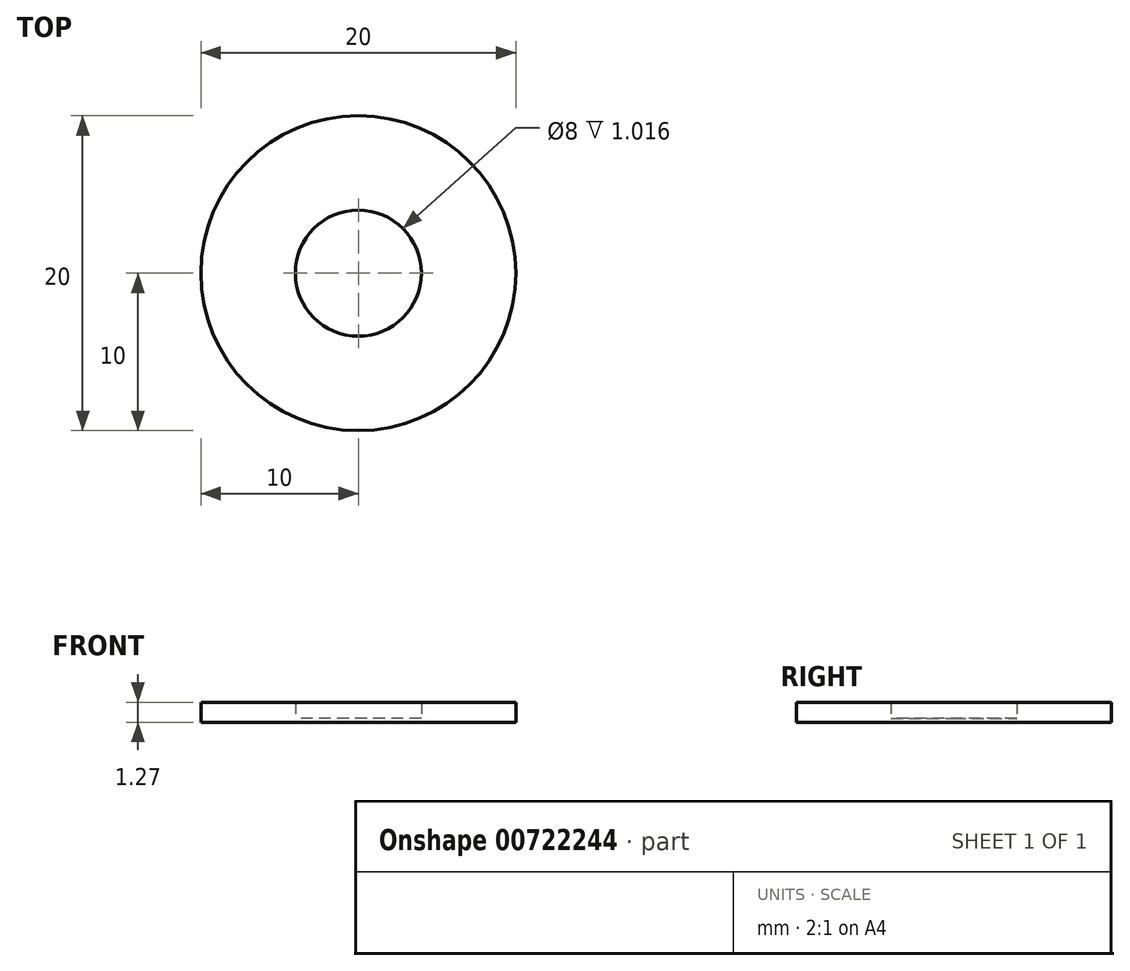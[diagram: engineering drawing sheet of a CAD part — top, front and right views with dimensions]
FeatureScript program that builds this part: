
annotation { "Feature Type Name" : "Feature", "Feature Type Description" : "" }
export const myFeature = defineFeature(function(context is Context, id is Id, definition is map)
    precondition{}
    {
        {
            var Q0;
            Q0=qCreatedBy(makeId("Top.planeOp"),FACE);
            var sketch = newSketch(context, id + "F0", { "sketchPlane" : qUnion([Q0])});
            skCircle(sketch, "E0", {"center": v(0, 0) * mm, "radius": 10 * mm});
            skCircle(sketch, "E1", {"center": v(0, 0) * mm, "radius": 4 * mm});
            skSolve(sketch);
        }
        {
            var Q0;
            Q0=qSketchRegion(id+"F0",true);
            var Q1;
            Q1=makeQuery(id+"F0.imprint","IMPRINT",FACE,{"disambiguationData":[TD([[makeQuery(id+"F0.imprint","IMPRINT",EDGE,{"derivedFrom":sQuery(id+"F0.wireOp",EDGE,"E0")}),1.0]])]});
            extrude(context, id + "F1", {"entities" : qUnion([Q0, Q1]), "depth" : 1.27 * mm, "offsetDistance" : 25.4 * mm});
        }
        {
            var Q0;
            Q0=makeQuery(id+"F0.imprint","IMPRINT",FACE,{"disambiguationData":[TD([[makeQuery(id+"F0.imprint","IMPRINT",EDGE,{"derivedFrom":sQuery(id+"F0.wireOp",EDGE,"E1")}),1.0]])]});
            extrude(context, id + "F2", {"entities" : qUnion([Q0]), "operationType" : NewBodyOperationType.ADD, "depth" : 0.25 * mm, "offsetDistance" : 25.4 * mm});
        }
    });
